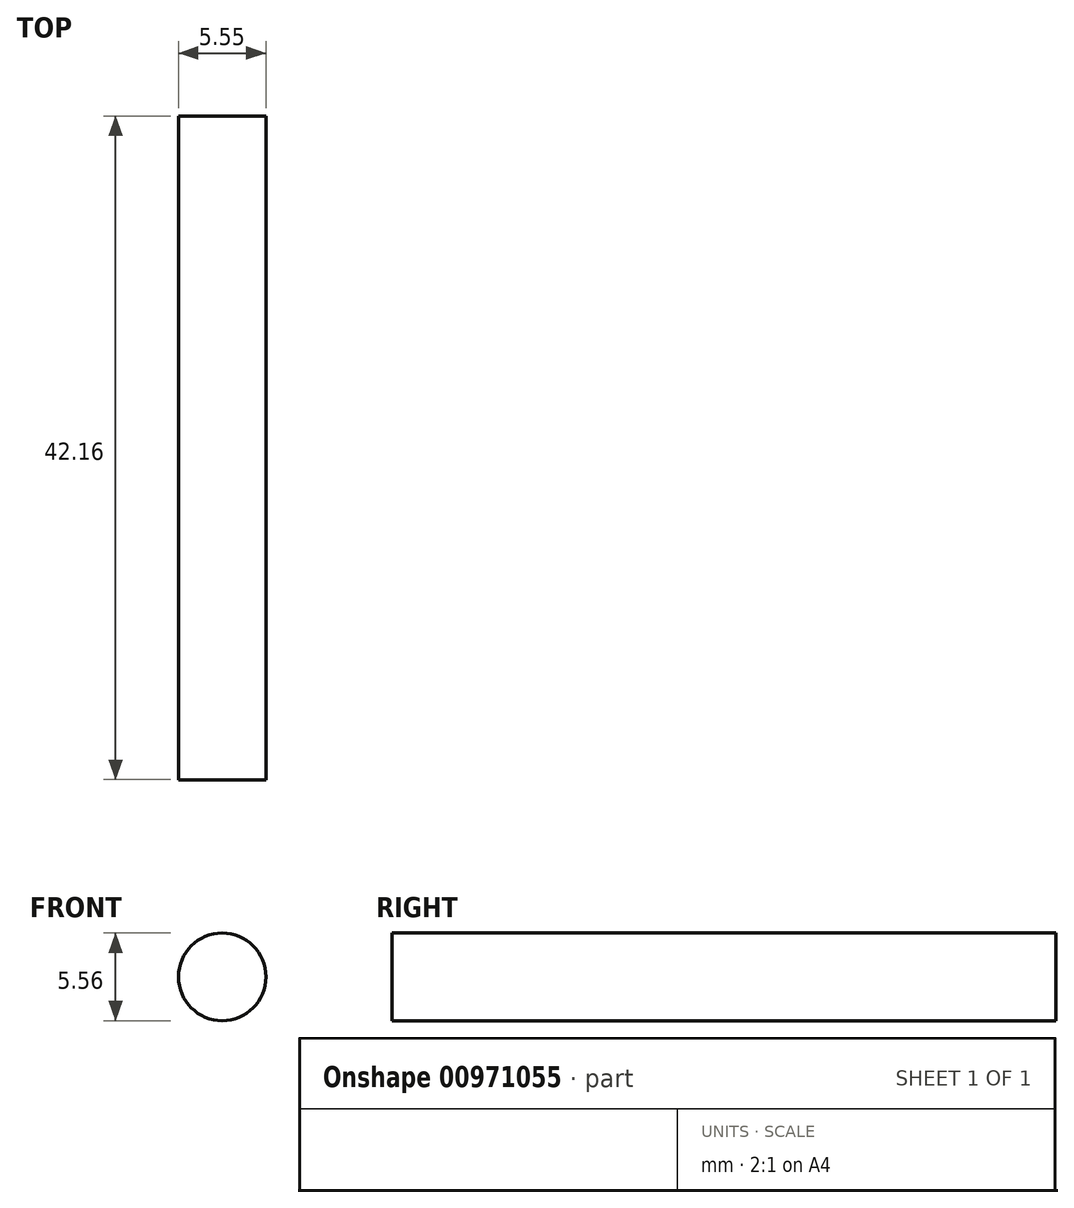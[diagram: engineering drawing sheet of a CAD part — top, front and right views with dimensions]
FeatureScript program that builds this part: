
annotation { "Feature Type Name" : "Feature", "Feature Type Description" : "" }
export const myFeature = defineFeature(function(context is Context, id is Id, definition is map)
    precondition{}
    {
        {
            var Q0;
            Q0=qCreatedBy(makeId("Front.planeOp"),FACE);
            var sketch = newSketch(context, id + "F0", { "sketchPlane" : qUnion([Q0])});
            skCircle(sketch, "E0", {"center": v(39.34, -37.14) * mm, "radius": 2.78 * mm});
            skSolve(sketch);
        }
        {
            var Q0;
            Q0=makeQuery(id+"F0.imprint","IMPRINT",FACE,{"disambiguationData":[TD([[makeQuery(id+"F0.imprint","IMPRINT",EDGE,{"derivedFrom":sQuery(id+"F0.wireOp",EDGE,"E0")}),1.0]])]});
            extrude(context, id + "F1", {"entities" : qUnion([Q0]), "depth" : 42.16 * mm, "offsetDistance" : 25.4 * mm});
        }
    });
